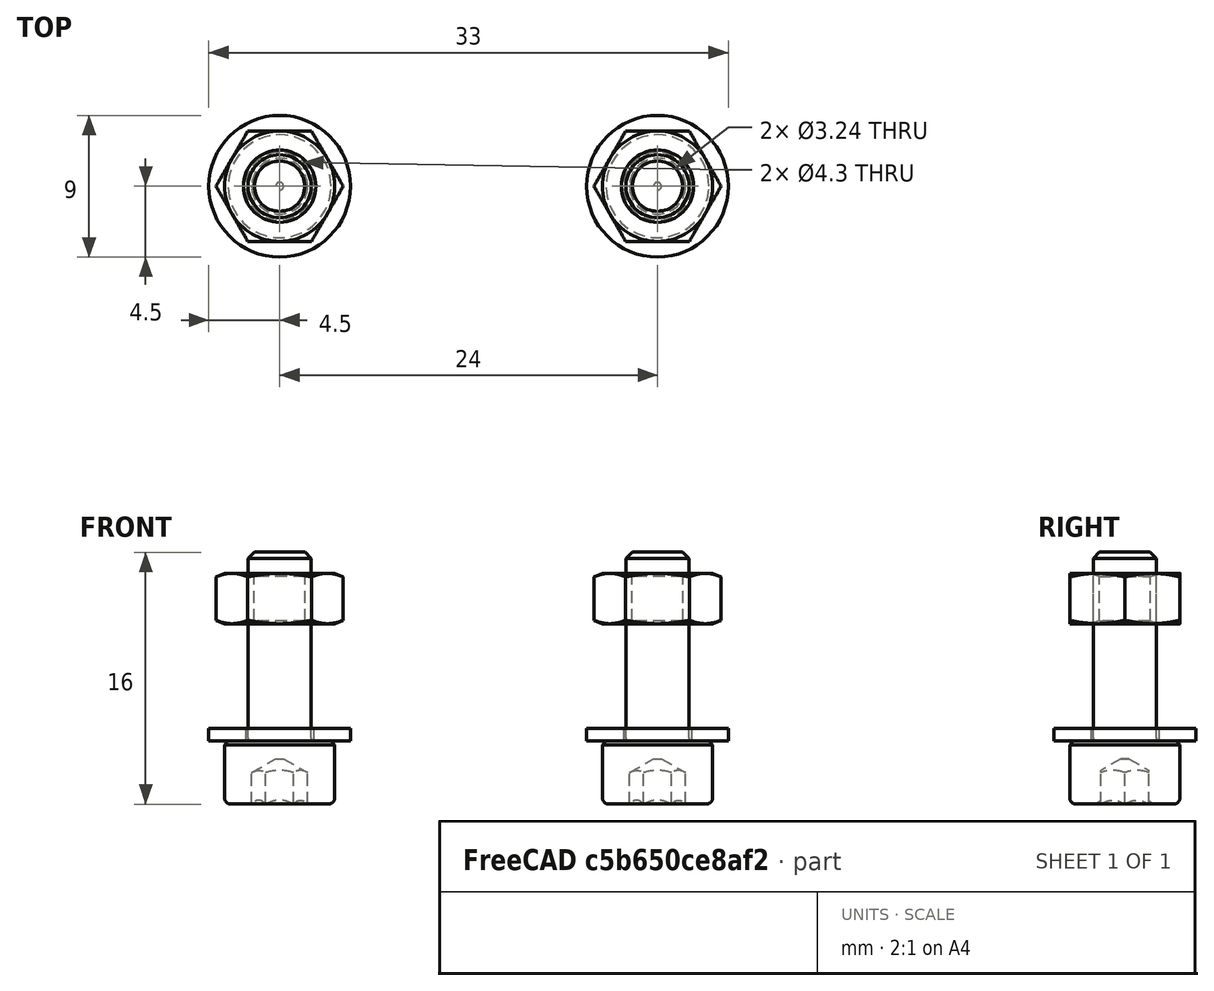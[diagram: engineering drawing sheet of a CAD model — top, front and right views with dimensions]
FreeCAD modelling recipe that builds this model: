
FCSTD DOCUMENT  (FreeCAD 0.20R29177 +426 (Git))
Label: ASM_TableRoller
License: All rights reserved
LicenseURL: http://en.wikipedia.org/wiki/All_rights_reserved
objects: Part::FeaturePython×6, App::DocumentObjectGroup×4, App::Link×2, PartDesign::CoordinateSystem×1, App::FeaturePython×1, App::Part×1
note: 7 computed .brp shape members not serialized (recipe doc carries the construction recipe); baked Part::Feature solids carry a one-line shape summary decoded from their .brp
EXTERNAL_REF file=TableRollerBase.FCStd obj=LCS_Origin
EXTERNAL_REF file=TableRollerBase.FCStd obj=Assembly
EXTERNAL_REF file=TableRollerBase.FCStd obj=Pad
EXTERNAL_REF file=TableRollerBase.FCStd obj=Sketch003
EXTERNAL_REF file=Params.FCStd obj=Spreadsheet
EXTERNAL_REF file=ASM_RollerShaft.FCStd obj=LCS_Origin
EXTERNAL_REF file=TableRollerBase.FCStd obj=LCS_Axle
EXTERNAL_REF file=ASM_RollerShaft.FCStd obj=Assembly

FEATURE [App::DocumentObjectGroup] Parts
FEATURE [PartDesign::CoordinateSystem] LCS_Origin
  AttacherType = Attacher::AttachEngine3D
  MapMode = 2
  Support = -> [X_Axis]
FEATURE [App::FeaturePython] Variables  # WARN: FeaturePython — macro-defined, semantics opaque (R4)
  Type = App::PropertyContainer
FEATURE [App::DocumentObjectGroup] Constraints
FEATURE [App::DocumentObjectGroup] Configurations
FEATURE [App::Link] TableRollerBase
  AttachedBy = #LCS_Origin
  AttachedTo = Parent Assembly#LCS_Origin
  LinkedObject = -> <external TableRollerBase.FCStd>#Assembly
  SolverId = Asm4EE
  expr: Placement = LCS_Origin.Placement * AttachmentOffset * TableRollerBase#LCS_Origin.Placement ^ -1
FEATURE [Part::FeaturePython] Nut  label="M4-Nut"  # Fasteners workbench fastener (typed FeaturePython)
  Placement = pos=(-12,12,4) rot=(0,0,1;0rad)
  baseObject = -> <external TableRollerBase.FCStd>#Sketch003 [Edge2]
  diameter = 6
  invert = false
  leftHanded = false
  matchOuter = false
  offset = 4
  thread = false
  type = 7
  expr: offset = <<TableRollerBase>>#Pad.Length - 3mm
FEATURE [Part::FeaturePython] Washer  label="M4-Washer"  # Fasteners workbench fastener (typed FeaturePython)
  Placement = pos=(-12,12,-2.656) rot=(-1,0,0;3.14159rad)
  baseObject = -> <external TableRollerBase.FCStd>#Sketch003 [Edge2]
  diameter = 5
  invert = true
  matchOuter = false
  offset = 2.656
  type = 3
  expr: offset = <<Params>>#<<Params>>.SheetMetalThickness
FEATURE [Part::FeaturePython] Nut001  label="M4-Nut001"  # Fasteners workbench fastener (typed FeaturePython)
  Placement = pos=(12,12,4) rot=(0,0,1;0rad)
  baseObject = -> <external TableRollerBase.FCStd>#Sketch003 [Edge1]
  diameter = 6
  invert = false
  leftHanded = false
  matchOuter = false
  offset = 4
  thread = false
  type = 7
  expr: offset = <<TableRollerBase>>#Pad.Length - 3mm
FEATURE [Part::FeaturePython] Washer001  label="M4-Washer001"  # Fasteners workbench fastener (typed FeaturePython)
  Placement = pos=(12,12,-2.656) rot=(-1,0,0;3.14159rad)
  baseObject = -> <external TableRollerBase.FCStd>#Sketch003 [Edge1]
  diameter = 5
  invert = true
  matchOuter = false
  offset = 2.656
  type = 3
  expr: offset = <<Params>>#<<Params>>.SheetMetalThickness
FEATURE [App::Link] ASM_RollerShaft
  AttachedBy = #LCS_Origin
  AttachedTo = TableRollerBase#LCS_Axle
  AttachmentOffset = pos=(0,0,0) rot=(1,0,0;1.5708rad)
  LinkPlacement = pos=(0,0,5) rot=(1,0,0;1.5708rad)
  LinkedObject = -> <external ASM_RollerShaft.FCStd>#Assembly
  Placement = pos=(0,0,5) rot=(1,0,0;1.5708rad)
  SolverId = Asm4EE
  expr: Placement = TableRollerBase.Placement * TableRollerBase#LCS_Axle.Placement * AttachmentOffset * ASM_RollerShaft#LCS_Origin.Placement ^ -1
FEATURE [Part::FeaturePython] Screw  label="M4x12-Screw"  # Fasteners workbench fastener (typed FeaturePython)
  Placement = pos=(12,12,-3.456) rot=(-1,0,0;3.14159rad)
  baseObject = -> Washer001 [Edge1]
  diameter = 5
  invert = false
  leftHanded = false
  length = 3
  lengthCustom = 12
  matchOuter = false
  offset = 0
  thread = false
  type = 34
FEATURE [Part::FeaturePython] Screw001  label="M4x12-Screw001"  # Fasteners workbench fastener (typed FeaturePython)
  Placement = pos=(-12,12,-3.456) rot=(-1,0,0;3.14159rad)
  baseObject = -> Washer [Edge1]
  diameter = 5
  invert = false
  leftHanded = false
  length = 3
  lengthCustom = 12
  matchOuter = false
  offset = 0
  thread = false
  type = 34
FEATURE [App::DocumentObjectGroup] Fasteners
  Group = -> [Nut,Washer,Nut001,Washer001,Screw,Screw001]
FEATURE [App::Part] Assembly
  AssemblyType = Part::Link
  Group = -> [LCS_Origin,Variables,Constraints,Configurations,TableRollerBase,Fasteners,Nut,Washer,Nut001,Washer001,ASM_RollerShaft,Screw,Screw001]
  Origin = -> Origin
  Type = Assembly

RESOLVED EXTERNAL PARTS (link-assembly join: the EXTERNAL_REF files above that resolve inside this repo's crawl, each included once):
---- part ASM_RollerShaft.FCStd = doc fcstd_6a988e584fd0 ----
FCSTD DOCUMENT  (FreeCAD 0.20R29177 +426 (Git))
Label: ASM_RollerShaft
License: All rights reserved
LicenseURL: http://en.wikipedia.org/wiki/All_rights_reserved
objects: App::DocumentObjectGroup×4, App::Link×3, Part::FeaturePython×2, PartDesign::CoordinateSystem×1, App::FeaturePython×1, App::Part×1
note: 3 computed .brp shape members not serialized (recipe doc carries the construction recipe); baked Part::Feature solids carry a one-line shape summary decoded from their .brp
EXTERNAL_REF file=Shaft.FCStd obj=LCS_1
EXTERNAL_REF file=Shaft.FCStd obj=Part
EXTERNAL_REF file=Bearing608.FCStd obj=LCS_axle
EXTERNAL_REF file=Bearing608.FCStd obj=Part
EXTERNAL_REF file=TableRollerTire.FCStd obj=LCS_Origin
EXTERNAL_REF file=TableRollerTire.FCStd obj=Assembly
EXTERNAL_REF file=Bearing608.FCStd obj=Chamfer

FEATURE [App::DocumentObjectGroup] Parts
FEATURE [PartDesign::CoordinateSystem] LCS_Origin
  AttacherType = Attacher::AttachEngine3D
  MapMode = 2
  Support = -> [X_Axis]
FEATURE [App::FeaturePython] Variables  # WARN: FeaturePython — macro-defined, semantics opaque (R4)
  Type = App::PropertyContainer
FEATURE [App::DocumentObjectGroup] Constraints
FEATURE [App::DocumentObjectGroup] Configurations
FEATURE [App::Link] DowelPin
  AssemblyType = Part::Link
  AttachedBy = #LCS_1
  AttachedTo = Parent Assembly#LCS_Origin
  LinkedObject = -> <external Shaft.FCStd>#Part
  SolverId = Asm4EE
  expr: Placement = LCS_Origin.Placement * AttachmentOffset * Shaft#LCS_1.Placement ^ -1
FEATURE [App::Link] Bearing608
  AssemblyType = Part::Link
  AttachedBy = #LCS_axle
  AttachedTo = DowelPin#LCS_1
  LinkedObject = -> <external Bearing608.FCStd>#Part
  SolverId = Asm4EE
  expr: Placement = DowelPin.Placement * Shaft#LCS_1.Placement * AttachmentOffset * Bearing608#LCS_axle.Placement ^ -1
FEATURE [App::Link] TableRollerTire
  AttachedBy = #LCS_Origin
  AttachedTo = Bearing608#LCS_axle
  LinkedObject = -> <external TableRollerTire.FCStd>#Assembly
  SolverId = Asm4EE
  expr: Placement = Bearing608.Placement * Bearing608#LCS_axle.Placement * AttachmentOffset * TableRollerTire#LCS_Origin.Placement ^ -1
FEATURE [Part::FeaturePython] Washer  label="M8-Washer"  # Fasteners workbench fastener (typed FeaturePython)
  Placement = pos=(0,-1e-15,-3.5) rot=(1,0,0;3.14159rad)
  baseObject = -> <external Bearing608.FCStd>#Chamfer [Edge11]
  diameter = 8
  invert = false
  matchOuter = true
  offset = 0
  type = 3
FEATURE [Part::FeaturePython] Washer001  label="M8-Washer001"  # Fasteners workbench fastener (typed FeaturePython)
  Placement = pos=(0,1e-15,3.5) rot=(0,0,1;0rad)
  baseObject = -> <external Bearing608.FCStd>#Chamfer [Edge1]
  diameter = 8
  invert = true
  matchOuter = true
  offset = 0
  type = 3
FEATURE [App::DocumentObjectGroup] Fasteners
  Group = -> [Washer,Washer001]
FEATURE [App::Part] Assembly
  AssemblyType = Part::Link
  Group = -> [LCS_Origin,Variables,Constraints,Configurations,DowelPin,Bearing608,Fasteners,TableRollerTire,Washer,Washer001]
  Origin = -> Origin
  Type = Assembly
---- part Params.FCStd = doc fcstd_b8f81ed59c9d ----
FCSTD DOCUMENT  (FreeCAD 0.20R29177 +426 (Git))
Label: Params
License: All rights reserved
LicenseURL: http://en.wikipedia.org/wiki/All_rights_reserved
objects: Spreadsheet::Sheet×1

FEATURE [Spreadsheet::Sheet] Spreadsheet  label="Params"
  cells = A1=DriveWheelWidth; B1(DriveWheelWidth)=10; D1=PlywoodThickness; E1(PlywoodThickness)=18.5; A2=DriveWheelMajorDiameter; B2(DriveWheelMajorDiameter)=52; D2=ExtensionArmCenterOffset; E2(ExtensionArmCenterOffset)=23; A3=DriveWheelCrown; B3(DriveWheelCrown)=2; D3=SheetMetalThickness; E3(SheetMetalThickness)=2.656; A4=DriveWheelTireThickness; B4(DriveWheelTireThickness)=3; D4=CeilingPlateDiameter; E4(CeilingPlateDiameter)=463; A6=DriveUnitAngle; B6(DriveUnitAngle)=30; D6=TableRollerMountHoleSpacing; E6(TableRollerMountHoleSpacing)=24; A7=DriveRadius; B7(DriveRadius)=280; D7=TableRollerMountHoleOffset; E7(TableRollerMountHoleOffset)=12; A8=DriveAdjMiddleOffset; B8(DriveAdjMiddleOffset)=90; D8=TableRollerDriveSupportRadius; E8(TableRollerDriveSupportRadius)=218; A9=RotationDriveOffset; B9(RotationDriveOffset)=29; D9=TableRollerSideRadius; E9(TableRollerSideRadius)=164; A10=FrontSkateOffset; B10(FrontSkateOffset)=350; D10=TableRollerDriveSupportAngle; E10(TableRollerDriveSupportAngle)=13.5; A11=RearSkateOffset; B11(RearSkateOffset)=150; D11=TableRollerSideAngle; E11(TableRollerSideAngle)=20; A13=CablePulleyDiameter; B13(CablePulleyDiameter)=120; D13=RoomWidth; E13(RoomWidth)=3650; D14=RoomLength; E14(RoomLength)=3650; A15=ExtensionDriverOffsetX; B15(ExtensionDriverOffsetX)=100; D15=RoomHeight; E15(RoomHeight)=2440; A16=ExtensionDriverOffsetY; B16(ExtensionDriverOffsetY)=-36
---- part TableRollerBase.FCStd = doc fcstd_24007bd8aee8 ----
FCSTD DOCUMENT  (FreeCAD 0.20R29177 +426 (Git))
Label: TableRollerBase
License: All rights reserved
LicenseURL: http://en.wikipedia.org/wiki/All_rights_reserved
objects: Sketcher::SketchObject×5, App::DocumentObjectGroup×3, PartDesign::CoordinateSystem×2, PartDesign::Pocket×2, App::FeaturePython×1, PartDesign::Pad×1, PartDesign::Hole×1, PartDesign::Groove×1, PartDesign::Body×1, App::Part×1
note: 18 computed .brp shape members not serialized (recipe doc carries the construction recipe); baked Part::Feature solids carry a one-line shape summary decoded from their .brp
EXTERNAL_REF file=Params.FCStd obj=Spreadsheet

FEATURE [App::DocumentObjectGroup] Parts
FEATURE [PartDesign::CoordinateSystem] LCS_Origin
  AttacherType = Attacher::AttachEngine3D
  MapMode = 2
  Support = -> [X_Axis]
FEATURE [App::FeaturePython] Variables  # WARN: FeaturePython — macro-defined, semantics opaque (R4)
  Type = App::PropertyContainer
FEATURE [App::DocumentObjectGroup] Constraints
FEATURE [App::DocumentObjectGroup] Configurations
FEATURE [Sketcher::SketchObject] Sketch
  AttachmentOffset = pos=(0,0,5) rot=(0,0,1;0rad)
  FullyConstrained = true
  MapMode = 5
  Placement = pos=(0,0,5) rot=(0,0,1;0rad)
  Support = -> [XY_Plane001]
  expr: .AttachmentOffset.Base.z = <<AxleSketch>>.Constraints.AxleOffset
  sketch-geometry (8):
    g0: ArcOfCircle CenterX=10.5 CenterY=1e-16 CenterZ=0 NormalX=0 NormalY=0 NormalZ=1 AngleXU=0 Radius=6 StartAngle=4.71239 EndAngle=7.85398
    g1: LineSegment StartX=0 StartY=5 StartZ=0 EndX=0 EndY=-5 EndZ=0
    g2: LineSegment StartX=0 StartY=5 StartZ=0 EndX=8 EndY=5 EndZ=0
    g3: LineSegment StartX=0 StartY=-5 StartZ=0 EndX=8 EndY=-5 EndZ=0
    g4: LineSegment StartX=8 StartY=-5 StartZ=0 EndX=9 EndY=-6 EndZ=0
    g5: LineSegment StartX=8 StartY=5 StartZ=0 EndX=9 EndY=6 EndZ=0
    g6: LineSegment StartX=9 StartY=6 StartZ=0 EndX=10.5 EndY=6 EndZ=0
    g7: LineSegment StartX=9 StartY=-6 StartZ=0 EndX=10.5 EndY=-6 EndZ=0
  constraints (22):
    c: DistanceX(g-1,g0) = 10.5
    c: PointOnObject(g1,g-2)
    c: Symmetric(g1,g1,g-1)
    c: Coincident(g2,g1)
    c: Horizontal(g2)
    c: Coincident(g3,g1)
    c: Horizontal(g3)
    c: Coincident(g4,g3)
    c: Coincident(g5,g2)
    c: Coincident(g6,g5)
    c: Horizontal(g6)
    c: Coincident(g7,g4)
    c: Horizontal(g7)
    c: Tangent(g0,g7) = -1.5708
    c: Tangent(g0,g6) = 1.5708
    c: Equal(g5,g4)
    c: Angle(g4,g-1) = 0.785398
    c: Equal(g7,g6)
    c: Equal(g2,g3)
    c: DistanceY(g1,g1) = 10
    c: DistanceY(g4,g5) = 12
    c: DistanceX(g2,g2) = 8
FEATURE [Sketcher::SketchObject] Sketch001
  FullyConstrained = true
  MapMode = 5
  Support = -> [XY_Plane001]
  sketch-geometry (11):
    g0: ArcOfCircle CenterX=-7 CenterY=6 CenterZ=0 NormalX=0 NormalY=0 NormalZ=1 AngleXU=0 Radius=15 StartAngle=1.5708 EndAngle=3.14159
    g1: LineSegment StartX=-7 StartY=21 StartZ=0 EndX=7 EndY=21 EndZ=0
    g2: ArcOfCircle CenterX=7 CenterY=6 CenterZ=0 NormalX=0 NormalY=0 NormalZ=1 AngleXU=0 Radius=15 StartAngle=1e-16 EndAngle=1.5708
    g3: LineSegment StartX=22 StartY=6 StartZ=0 EndX=22 EndY=-4.4e-15 EndZ=0
    g4: ArcOfCircle CenterX=7 CenterY=-4e-16 CenterZ=0 NormalX=0 NormalY=0 NormalZ=1 AngleXU=0 Radius=15 StartAngle=4.71239 EndAngle=6.28319
    g5: LineSegment StartX=7 StartY=-15 StartZ=0 EndX=-7 EndY=-15 EndZ=0
    g6: ArcOfCircle CenterX=-7 CenterY=-3e-16 CenterZ=0 NormalX=0 NormalY=0 NormalZ=1 AngleXU=0 Radius=15 StartAngle=3.14159 EndAngle=4.71239
    g7: LineSegment StartX=-22 StartY=-5.1e-15 StartZ=0 EndX=-22 EndY=6 EndZ=0
    g8: GeomPoint X=-22 Y=21 Z=0
    g9: GeomPoint X=22 Y=-15 Z=0
    g10: GeomPoint X=0 Y=-15 Z=0
  constraints (25):
    c: Tangent(g0,g1) = 1.5708
    c: Tangent(g1,g2) = 1.5708
    c: Tangent(g2,g3) = 1.5708
    c: Tangent(g3,g4) = 1.5708
    c: Tangent(g4,g5) = 1.5708
    c: Tangent(g5,g6) = 1.5708
    c: Tangent(g6,g7) = 1.5708
    c: Tangent(g7,g0) = 1.5708
    c: Horizontal(g1)
    c: Horizontal(g5)
    c: Vertical(g3)
    c: Vertical(g7)
    c: Equal(g0,g2)
    c: Equal(g2,g4)
    c: Equal(g4,g6)
    c: PointOnObject(g8,g1)
    c: PointOnObject(g8,g7)
    c: PointOnObject(g9,g3)
    c: PointOnObject(g9,g5)
    c: DistanceY(g4,g-1) = 15  'BaseBackOffset'
    c: PointOnObject(g10,g-2)
    c: Symmetric(g4,g5,g10)
    c: Radius(g2) = 15
    c: DistanceX(g0,g2) = 44  'BaseWidth'
    c: DistanceY(g5,g0) = 36
FEATURE [Sketcher::SketchObject] Sketch002  label="AxleSketch"
  FullyConstrained = true
  MapMode = 5
  Placement = pos=(0,0,0) rot=(1,0,0;1.5708rad)
  Support = -> [XZ_Plane001]
  expr: .Constraints.AxleOffset = <<Base>>.Length - 2mm
  sketch-geometry (1):
    g0: Circle CenterX=0 CenterY=5 CenterZ=0 NormalX=0 NormalY=0 NormalZ=1 AngleXU=0 Radius=4.1
  constraints (3):
    c: PointOnObject(g0,g-2)
    c: Diameter(g0) = 8.2
    c: DistanceY(g-1,g0) = 5  'AxleOffset'
FEATURE [Sketcher::SketchObject] Sketch003
  AttachmentOffset = pos=(12,12,0) rot=(0,0,1;0rad)
  FullyConstrained = true
  MapMode = 5
  Placement = pos=(12,12,0) rot=(0,0,1;0rad)
  Support = -> [XY_Plane001]
  expr: .AttachmentOffset.Base.x = <<Params>>#<<Params>>.TableRollerMountHoleSpacing / 2
  expr: .AttachmentOffset.Base.y = <<Params>>#<<Params>>.TableRollerMountHoleOffset
  expr: Constraints[4] = <<Params>>#<<Params>>.TableRollerMountHoleSpacing
  sketch-geometry (2):
    g0: Circle CenterX=0 CenterY=0 CenterZ=0 NormalX=0 NormalY=0 NormalZ=1 AngleXU=0 Radius=1.5
    g1: Circle CenterX=-24 CenterY=0 CenterZ=0 NormalX=0 NormalY=0 NormalZ=1 AngleXU=0 Radius=1.5
  constraints (5):
    c: Coincident(g0,g-1)
    c: Diameter(g0) = 3
    c: PointOnObject(g1,g-1)
    c: Equal(g1,g0)
    c: DistanceX(g1,g0) = 24
FEATURE [Sketcher::SketchObject] Sketch004
  AttachmentOffset = pos=(0,0,4) rot=(0,0,1;0rad)
  FullyConstrained = true
  MapMode = 2
  Placement = pos=(12,12,4) rot=(0,0,1;0rad)
  Support = -> [Sketch003]
  expr: .AttachmentOffset.Base.z = <<Base>>.Length - 3mm
  expr: Constraints[40] = <<Params>>#<<Params>>.TableRollerMountHoleSpacing
  sketch-geometry (14):
    g0: LineSegment StartX=4.21466 StartY=0 StartZ=0 EndX=2.10733 EndY=3.65 EndZ=0
    g1: LineSegment StartX=2.10733 StartY=3.65 StartZ=0 EndX=-2.10733 EndY=3.65 EndZ=0
    g2: LineSegment StartX=-2.10733 StartY=3.65 StartZ=0 EndX=-4.21466 EndY=-1.3e-15 EndZ=0
    g3: LineSegment StartX=-4.21466 StartY=-1.3e-15 StartZ=0 EndX=-2.10733 EndY=-3.65 EndZ=0
    g4: LineSegment StartX=-2.10733 StartY=-3.65 StartZ=0 EndX=2.10733 EndY=-3.65 EndZ=0
    g5: LineSegment StartX=2.10733 StartY=-3.65 StartZ=0 EndX=4.21466 EndY=0 EndZ=0
    g6: Circle CenterX=0 CenterY=0 CenterZ=0 NormalX=0 NormalY=0 NormalZ=1 AngleXU=0 Radius=4.21466
    g7: LineSegment StartX=-19.7853 StartY=0 StartZ=0 EndX=-21.8927 EndY=3.65 EndZ=0
    g8: LineSegment StartX=-21.8927 StartY=3.65 StartZ=0 EndX=-26.1073 EndY=3.65 EndZ=0
    g9: LineSegment StartX=-26.1073 StartY=3.65 StartZ=0 EndX=-28.2147 EndY=-1.2e-14 EndZ=0
    g10: LineSegment StartX=-28.2147 StartY=-1.2e-14 StartZ=0 EndX=-26.1073 EndY=-3.65 EndZ=0
    g11: LineSegment StartX=-26.1073 StartY=-3.65 StartZ=0 EndX=-21.8927 EndY=-3.65 EndZ=0
    g12: LineSegment StartX=-21.8927 StartY=-3.65 StartZ=0 EndX=-19.7853 EndY=0 EndZ=0
    g13: Circle CenterX=-24 CenterY=0 CenterZ=0 NormalX=0 NormalY=0 NormalZ=1 AngleXU=0 Radius=4.21466
  constraints (33):
    c: Coincident(g0,g1)
    c: Coincident(g1,g2)
    c: Coincident(g2,g3)
    c: Coincident(g3,g4)
    c: Coincident(g4,g5)
    c: Coincident(g5,g0)
    c: Equal(g0, g1-g5) x5
    c: PointOnObject(g0,g6)
    c: PointOnObject(g1,g6)
    c: PointOnObject(g2,g6)
    c: PointOnObject(g3,g6)
    c: PointOnObject(g4,g6)
    c: PointOnObject(g5,g6)
    c: Coincident(g6,g-1)
    c: Distance(g4,g0) = 7.3
    c: PointOnObject(g0,g-1)
    c: Coincident(g7,g8)
    c: Coincident(g8,g9)
    c: Coincident(g9,g10)
    c: Coincident(g10,g11)
    c: Coincident(g11,g12)
    c: Coincident(g12,g7)
    c: Equal(g7, g8-g12) x5
    c: PointOnObject(g7,g13)
    c: PointOnObject(g8,g13)
    c: PointOnObject(g9,g13)
    c: PointOnObject(g10,g13)
    c: PointOnObject(g11,g13)
    c: PointOnObject(g12,g13)
    c: PointOnObject(g13,g-1)
    c: PointOnObject(g7,g-1)
    c: Equal(g8,g1)
    c: DistanceX(g13,g6) = 24
FEATURE [PartDesign::CoordinateSystem] LCS_Axle
  AttacherType = Attacher::AttachEngine3D
  AttachmentOffset = pos=(0,0,5) rot=(0,0,1;0rad)
  MapMode = 2
  Placement = pos=(0,0,5) rot=(0,0,1;0rad)
  Support = -> [LCS_Origin]
  expr: .AttachmentOffset.Base.z = <<AxleSketch>>.Constraints.AxleOffset
FEATURE [PartDesign::Pad] Pad  label="Base"
  Direction = (0,0,1)
  Length = 7
  Length2 = 10
  Profile = -> Sketch001
  ReferenceAxis = -> Sketch001 [N_Axis]
  Type = 0
FEATURE [PartDesign::Pocket] Pocket001  label="RollerAxle"
  BaseFeature = -> Pad
  Direction = (0,1,2e-16)
  Length = 21
  Length2 = 5
  Midplane = true
  Profile = -> Sketch002
  ReferenceAxis = -> Sketch002 [N_Axis]
  Type = 0
FEATURE [PartDesign::Hole] Hole  label="BaseMountHole"
  BaseFeature = -> Pocket001
  CustomThreadClearance = 0
  Depth = 154.21
  DepthType = 1
  Diameter = 4.5
  DrillForDepth = false
  DrillPoint = 1
  DrillPointAngle = 118
  HoleCutCountersinkAngle = 90
  HoleCutCustomValues = false
  HoleCutDepth = 0
  HoleCutDiameter = 6.1
  HoleCutType = 0
  ModelThread = false
  Profile = -> Sketch003
  Reversed = true
  Tapered = false
  TaperedAngle = 90
  ThreadClass = 0
  ThreadDepth = 154.21
  ThreadDepthType = 0
  ThreadDirection = 0
  ThreadFit = 0
  ThreadSize = 11
  ThreadType = 1
  Threaded = false
  UseCustomThreadClearance = false
FEATURE [PartDesign::Pocket] Pocket002  label="BaseMountNutPocket"
  BaseFeature = -> Hole
  Direction = (0,0,-1)
  Length = 5
  Length2 = 5
  Profile = -> Sketch004
  ReferenceAxis = -> Sketch004 [N_Axis]
  Reversed = true
  Type = 1
FEATURE [PartDesign::Groove] Groove  label="RollerSlot"
  Angle = 360
  Axis = (0,1,0)
  Base = (0,0,5)
  BaseFeature = -> Pocket002
  Profile = -> Sketch
  ReferenceAxis = -> Sketch [V_Axis]
FEATURE [PartDesign::Body] Body
  Group = -> [Pad,Sketch,Sketch001,Sketch002,Pocket001,Sketch003,Hole,Sketch004,Pocket002,Groove]
  Origin = -> Origin001
  Tip = -> Groove
FEATURE [App::Part] Assembly
  AssemblyType = Part::Link
  Group = -> [LCS_Origin,Variables,Constraints,Configurations,Body,LCS_Axle]
  Origin = -> Origin
  Type = Assembly
